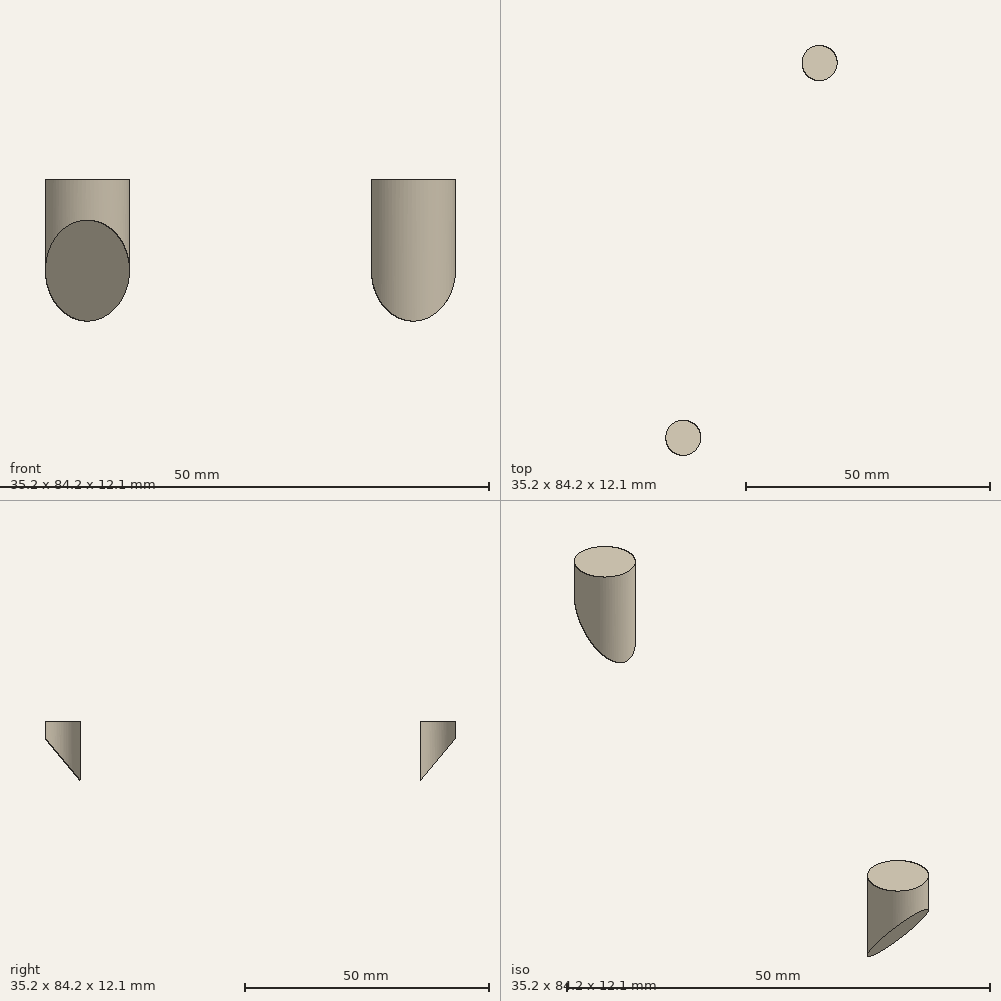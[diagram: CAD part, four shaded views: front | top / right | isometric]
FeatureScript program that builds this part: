
annotation { "Feature Type Name" : "Feature", "Feature Type Description" : "" }
export const myFeature = defineFeature(function(context is Context, id is Id, definition is map)
    precondition{}
    {
        {
            var Q0;
            Q0=qCreatedBy(makeId("Right.planeOp"),FACE);
            var sketch = newSketch(context, id + "F0", { "sketchPlane" : qUnion([Q0])});
            skCircle(sketch, "E0", {"center": v(0, 0) * mm, "radius": 30 * mm});
            skSolve(sketch);
        }
        {
            var Q0;
            Q0 = qSketchRegion(id + "F0", true);
            extrude(context, id + "F1", {"entities" : qUnion([Q0]), "endBound" : BoundingType.SYMMETRIC, "depth" : 30 * mm, "offsetDistance" : 25 * mm});
        }
        {
            var Q0;
            Q0=qCreatedBy(makeId("Right.planeOp"),FACE);
            var sketch = newSketch(context, id + "F2", { "sketchPlane" : qUnion([Q0])});
            skLineSegment(sketch, "E1", {"start": v(-45, 40) * mm, "end": v(45, 40) * mm});
            skLineSegment(sketch, "E2", {"start": v(45, 40) * mm, "end": v(0, -14) * mm});
            skLineSegment(sketch, "E3", {"start": v(0, -14) * mm, "end": v(-45, 40) * mm});
            skSolve(sketch);
        }
        {
            var Q0;
            Q0=makeQuery(id+"F2.imprint","IMPRINT",FACE,{"disambiguationData":[TD([[makeQuery(id+"F2.imprint","IMPRINT",EDGE,{"derivedFrom":sQuery(id+"F2.wireOp",EDGE,"E1")}),-1.0]])]});
            extrude(context, id + "F3", {"entities" : qUnion([Q0]), "operationType" : NewBodyOperationType.ADD, "endBound" : BoundingType.SYMMETRIC, "depth" : 42 * mm, "offsetDistance" : 25 * mm});
        }
        {
            var Q0;
            Q0=makeQuery(id+"F3.opExtrude","SWEPT_FACE",FACE,{"disambiguationData":[OSD([sQuery(id+"F2.wireOp",EDGE,"E1")])]});
            var sketch = newSketch(context, id + "F4", { "sketchPlane" : qUnion([Q0])});
            skCircle(sketch, "E4", {"center": v(-14, 38.5) * mm, "radius": 3.61 * mm});
            skCircle(sketch, "E5.MirrorC", {"center": v(14, 38.5) * mm, "radius": 3.61 * mm});
            skCircle(sketch, "E6.MirrorC", {"center": v(14, -38.5) * mm, "radius": 3.61 * mm});
            skCircle(sketch, "E7.MirrorC", {"center": v(-14, -38.5) * mm, "radius": 3.61 * mm});
            skSolve(sketch);
        }
        {
            var Q0;
            Q0=makeQuery(id+"F4.imprint","IMPRINT",FACE,{"disambiguationData":[TD([[makeQuery(id+"F4.imprint","IMPRINT",EDGE,{"derivedFrom":sQuery(id+"F4.wireOp",EDGE,"E4")}),1.0]])]});
            var Q1;
            Q1=makeQuery(id+"F4.imprint","IMPRINT",FACE,{"disambiguationData":[TD([[makeQuery(id+"F4.imprint","IMPRINT",EDGE,{"derivedFrom":sQuery(id+"F4.wireOp",EDGE,"E5.MirrorC")}),-1.0]])]});
            var Q2;
            Q2=makeQuery(id+"F4.imprint","IMPRINT",FACE,{"disambiguationData":[TD([[makeQuery(id+"F4.imprint","IMPRINT",EDGE,{"derivedFrom":sQuery(id+"F4.wireOp",EDGE,"E7.MirrorC")}),-1.0]])]});
            var Q3;
            Q3=makeQuery(id+"F4.imprint","IMPRINT",FACE,{"disambiguationData":[TD([[makeQuery(id+"F4.imprint","IMPRINT",EDGE,{"derivedFrom":sQuery(id+"F4.wireOp",EDGE,"E6.MirrorC")}),1.0]])]});
            extrude(context, id + "F5", {"entities" : qUnion([Q0, Q1, Q2, Q3]), "operationType" : NewBodyOperationType.REMOVE, "endBound" : BoundingType.THROUGH_ALL, "oppositeDirection" : true, "depth" : 25 * mm, "offsetDistance" : 25 * mm});
        }
        {
            var Q0;
            Q0=qCreatedBy(makeId("Front.planeOp"),FACE);
            var sketch = newSketch(context, id + "F6", { "sketchPlane" : qUnion([Q0])});
            skLineSegment(sketch, "E8", {"start": v(-11, -30) * mm, "end": v(11, -30) * mm});
            skLineSegment(sketch, "E9", {"start": v(11, -30) * mm, "end": v(0, -19) * mm});
            skLineSegment(sketch, "E10", {"start": v(0, -19) * mm, "end": v(-11, -30) * mm});
            skLineSegment(sketch, "E11", {"start": v(0, 0) * mm, "end": v(55.73, 0) * mm});
            skSolve(sketch);
        }
        {
            var Q0;
            Q0 = qSketchRegion(id + "F6", true);
            var Q1;
            Q1=sQuery(id+"F6.wireOp",EDGE,"E11");
            revolve(context, id + "F7", {"operationType" : NewBodyOperationType.REMOVE, "surfaceOperationType" : NewSurfaceOperationType.NEW, "entities" : qUnion([Q0]), "axis" : qUnion([Q1]), "revolveType" : RevolveType.FULL, "oppositeDirection" : true});
        }
    });
